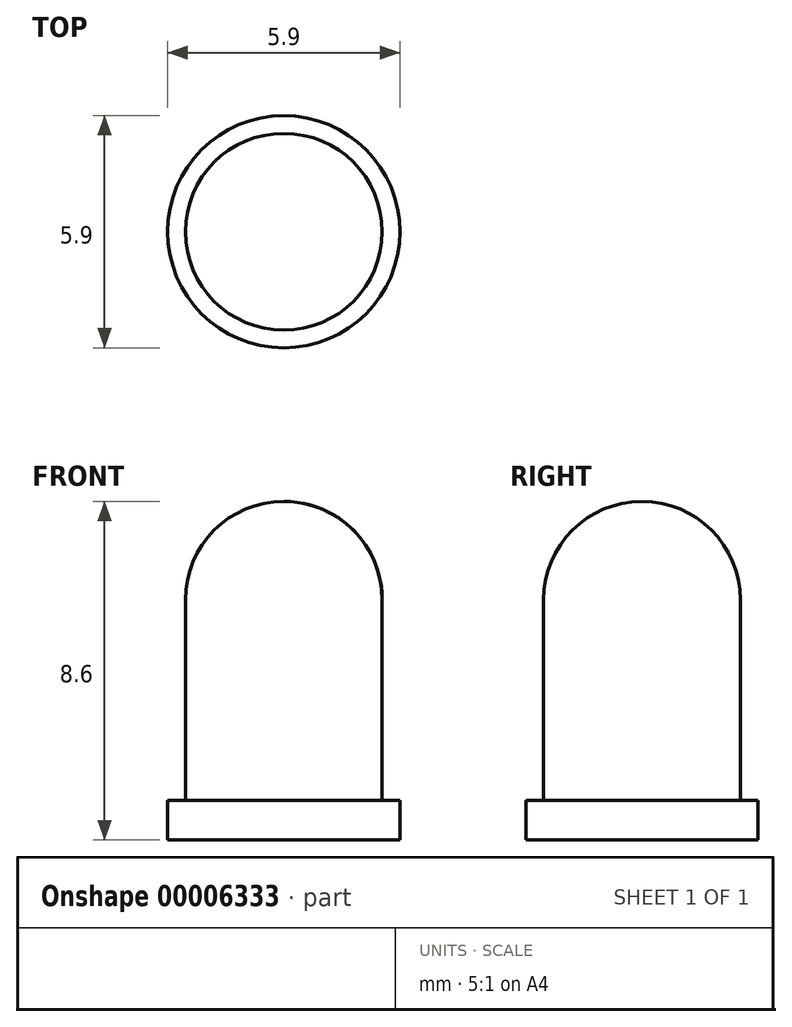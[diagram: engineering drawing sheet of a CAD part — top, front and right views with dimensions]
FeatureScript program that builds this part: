
annotation { "Feature Type Name" : "Feature", "Feature Type Description" : "" }
export const myFeature = defineFeature(function(context is Context, id is Id, definition is map)
    precondition{}
    {
        {
            var Q0;
            Q0=qCreatedBy(makeId("Top.planeOp"),FACE);
            var sketch = newSketch(context, id + "F0", { "sketchPlane" : qUnion([Q0])});
            skCircle(sketch, "E0", {"center": v(0, 0) * mm, "radius": 2.95 * mm});
            skSolve(sketch);
        }
        {
            var Q0;
            Q0=makeQuery(id+"F0.imprint","IMPRINT",FACE,{"disambiguationData":[TD([[makeQuery(id+"F0.imprint","IMPRINT",EDGE,{"derivedFrom":sQuery(id+"F0.wireOp",EDGE,"E0")}),1.0]])]});
            extrude(context, id + "F1", {"entities" : qUnion([Q0]), "depth" : 1 * mm});
        }
        {
            var Q0;
            Q0=qCreatedBy(makeId("Front.planeOp"),FACE);
            var sketch = newSketch(context, id + "F2", { "sketchPlane" : qUnion([Q0])});
            skLineSegment(sketch, "E1", {"start": v(0, 1) * mm, "end": v(2.5, 1) * mm});
            skLineSegment(sketch, "E2", {"start": v(2.5, 1) * mm, "end": v(2.5, 6.1) * mm});
            skLineSegment(sketch, "E3", {"start": v(0, 8.6) * mm, "end": v(0, 8.6) * mm});
            skLineSegment(sketch, "E4", {"start": v(0, 8.6) * mm, "end": v(0, 1) * mm});
            skPoint(sketch, "E5.visualSharp", {"position": v(2.5, 8.6) * mm});
            skArc(sketch, "E5.filletArc", {"start": v(2.5, 6.1) * mm, "mid": v(1.77, 7.87) * mm, "end": v(0, 8.6) * mm});
            skSolve(sketch);
        }
        {
            var Q0;
            Q0=makeQuery(id+"F2.imprint","IMPRINT",FACE,{"disambiguationData":[TD([[makeQuery(id+"F2.imprint","IMPRINT",EDGE,{"derivedFrom":sQuery(id+"F2.wireOp",EDGE,"E1")}),1.0]])]});
            var Q1;
            Q1=sQuery(id+"F2.wireOp",EDGE,"E4");
            revolve(context, id + "F3", {"operationType" : NewBodyOperationType.ADD, "entities" : qUnion([Q0]), "axis" : qUnion([Q1]), "revolveType" : RevolveType.FULL});
        }
    });
